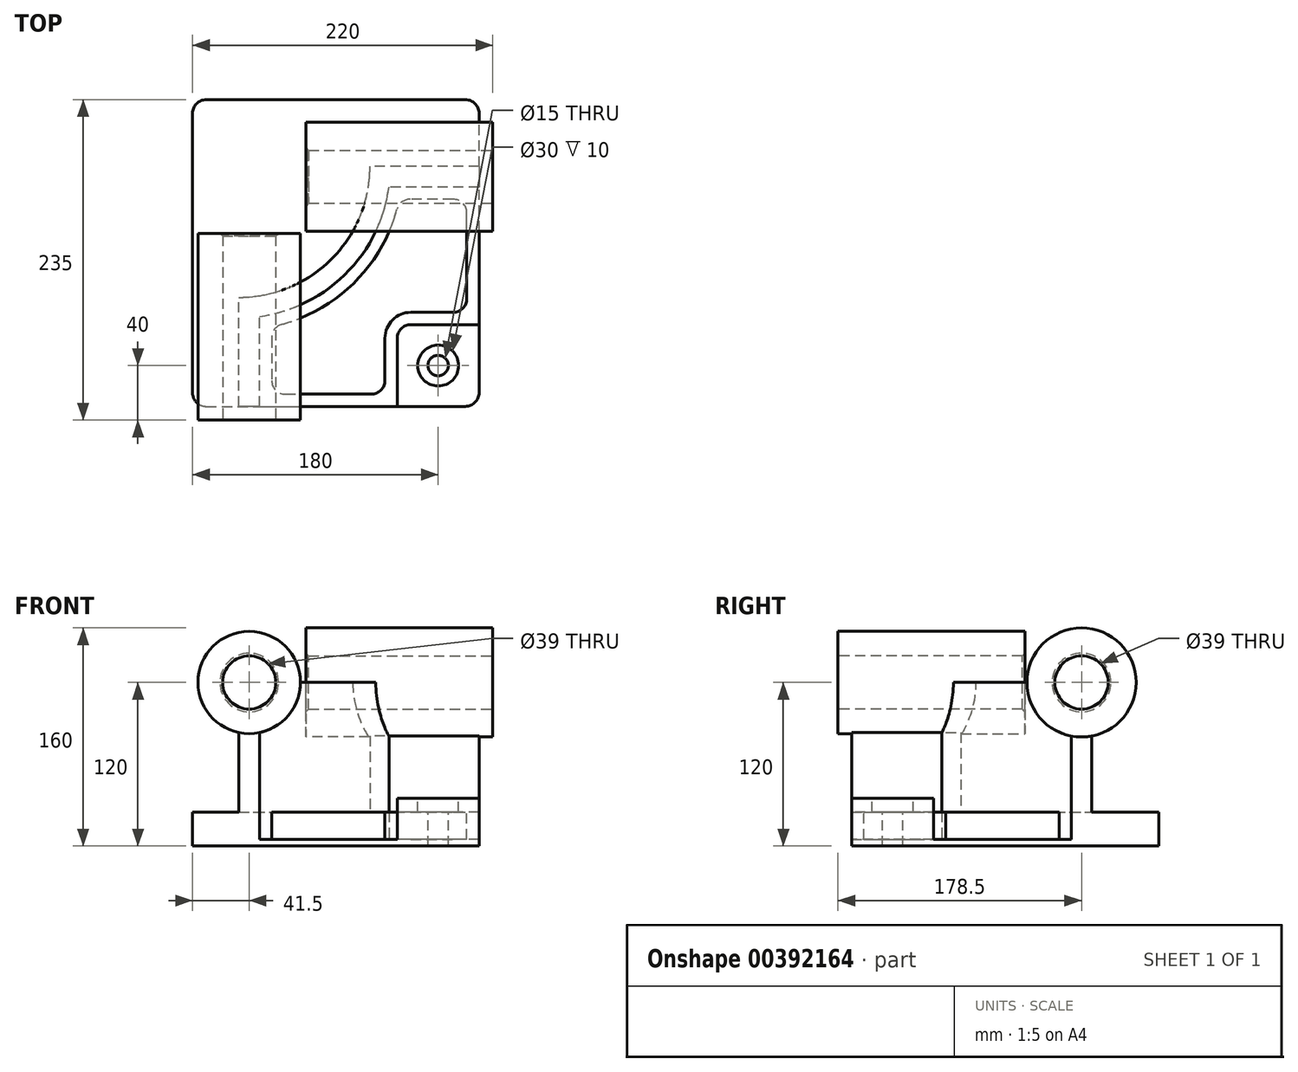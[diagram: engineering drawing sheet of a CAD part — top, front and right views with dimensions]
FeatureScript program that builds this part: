
annotation { "Feature Type Name" : "Feature", "Feature Type Description" : "" }
export const myFeature = defineFeature(function(context is Context, id is Id, definition is map)
    precondition{}
    {
        {
            var Q0;
            Q0=qCreatedBy(makeId("Top.planeOp"),FACE);
            var sketch = newSketch(context, id + "F0", { "sketchPlane" : qUnion([Q0])});
            skLineSegment(sketch, "E0.bottom", {"start": v(-105, -112.5) * mm, "end": v(105, -112.5) * mm});
            skLineSegment(sketch, "E0.top", {"start": v(-105, 112.5) * mm, "end": v(105, 112.5) * mm});
            skLineSegment(sketch, "E0.left", {"start": v(-105, -112.5) * mm, "end": v(-105, 112.5) * mm});
            skLineSegment(sketch, "E0.right", {"start": v(105, -112.5) * mm, "end": v(105, 112.5) * mm});
            skPoint(sketch, "E0.middle", {"position": v(0, 0) * mm});
            skSolve(sketch);
        }
        {
            var Q0;
            Q0=makeQuery(id+"F0.imprint","IMPRINT",FACE,{"disambiguationData":[TD([[makeQuery(id+"F0.imprint","IMPRINT",EDGE,{"derivedFrom":sQuery(id+"F0.wireOp",EDGE,"E0.bottom")}),1.0]])]});
            extrude(context, id + "F1", {"entities" : qUnion([Q0]), "depth" : 25 * mm});
        }
        {
            var Q0;
            Q0=makeQuery(id+"F1.opExtrude","CAP_FACE",FACE,{"disambiguationData":[OSD([sQuery(id+"F0.wireOp",EDGE,"E0.bottom"),sQuery(id+"F0.wireOp",EDGE,"E0.top"),sQuery(id+"F0.wireOp",EDGE,"E0.left"),sQuery(id+"F0.wireOp",EDGE,"E0.right")])],"isStart":false});
            var sketch = newSketch(context, id + "F2", { "sketchPlane" : qUnion([Q0])});
            skLineSegment(sketch, "E1", {"start": v(-71, -112.5) * mm, "end": v(-71, -32.5) * mm});
            skLineSegment(sketch, "E2", {"start": v(105, 63.5) * mm, "end": v(25, 63.5) * mm});
            skArc(sketch, "E3", {"start": v(-71, -32.5) * mm, "mid": v(-3.12, -4.38) * mm, "end": v(25, 63.5) * mm});
            skLineSegment(sketch, "E4", {"start": v(-71, 63.5) * mm, "end": v(25, 63.5) * mm, "construction": true});
            skLineSegment(sketch, "E5", {"start": v(-71, 63.5) * mm, "end": v(-71, -32.5) * mm, "construction": true});
            skLineSegment(sketch, "E6.0", {"start": v(105, 48.5) * mm, "end": v(38.98, 48.5) * mm});
            skArc(sketch, "E6.1", {"start": v(-56, -46.48) * mm, "mid": v(7.49, -14.99) * mm, "end": v(38.98, 48.5) * mm});
            skLineSegment(sketch, "E6.2", {"start": v(-56, -112.5) * mm, "end": v(-56, -46.48) * mm});
            skLineSegment(sketch, "E7.0", {"start": v(105, -112.5) * mm, "end": v(105, 112.5) * mm});
            skSolve(sketch);
        }
        {
            var Q0;
            {var subQ0=sQuery(id+"F2.wireOp",EDGE,"E3");Q0=makeQuery(id+"F2.imprint","IMPRINT",FACE,{"disambiguationData":[TD([[makeQuery(id+"F2.imprint","IMPRINT",EDGE,{"derivedFrom":subQ0}),-1.0]])]});}
            extrude(context, id + "F3", {"entities" : qUnion([Q0]), "operationType" : NewBodyOperationType.ADD, "depth" : 95 * mm});
        }
        {
            var Q0;
            {var subQ0=sQuery(id+"F0.wireOp",EDGE,"E0.bottom");Q0=makeQuery(id+"F3.boolean.opBoolean","MERGE",FACE,{"derivedFrom":[makeQuery(id+"F1.opExtrude","SWEPT_FACE",FACE,{"disambiguationData":[OSD([subQ0])]}),makeQuery(id+"F3.opExtrude","SWEPT_FACE",FACE,{"disambiguationData":[OSD([subQ0])]})]});}
            var sketch = newSketch(context, id + "F4", { "sketchPlane" : qUnion([Q0])});
            skCircle(sketch, "E8", {"center": v(-63.5, 120) * mm, "radius": 37.5 * mm});
            skSolve(sketch);
        }
        {
            var Q0;
            Q0 = qSketchRegion(id + "F4", true);
            var Q1;
            {var subQ1=sQuery(id+"F0.wireOp",EDGE,"E0.bottom");var subQ6=makeQuery(id+"F3.opExtrude","CAP_EDGE",EDGE,{"disambiguationData":[OSD([subQ1])],"isStart":false});Q1=makeQuery(id+"F4.imprint","IMPRINT",FACE,{"disambiguationData":[TD([[makeQuery(id+"F4.imprint","IMPRINT",EDGE,{"derivedFrom":subQ6}),1.0]])]});}
            extrude(context, id + "F5", {"entities" : qUnion([Q0, Q1]), "operationType" : NewBodyOperationType.ADD, "depth" : 10 * mm, "hasSecondDirection" : true, "secondDirectionOppositeDirection" : true, "secondDirectionDepth" : (137 - 10) * mm});
        }
        {
            var Q0;
            Q0=makeQuery(id+"F3.boolean.opBoolean","MERGE",FACE,{"derivedFrom":[makeQuery(id+"F1.opExtrude","SWEPT_FACE",FACE,{"disambiguationData":[OSD([sQuery(id+"F0.wireOp",EDGE,"E0.right")])]}),makeQuery(id+"F3.opExtrude","SWEPT_FACE",FACE,{"disambiguationData":[OSD([sQuery(id+"F2.wireOp",EDGE,"E7.0")])]})]});
            var sketch = newSketch(context, id + "F6", { "sketchPlane" : qUnion([Q0])});
            skCircle(sketch, "E9", {"center": v(56, 120) * mm, "radius": 40 * mm});
            skSolve(sketch);
        }
        {
            var Q0;
            Q0 = qSketchRegion(id + "F6", true);
            extrude(context, id + "F7", {"entities" : qUnion([Q0]), "operationType" : NewBodyOperationType.ADD, "depth" : 10 * mm, "hasSecondDirection" : true, "secondDirectionOppositeDirection" : true, "secondDirectionDepth" : (137 - 10) * mm});
        }
        {
            var Q0;
            {var subQ0=sQuery(id+"F0.wireOp",EDGE,"E0.right");var subQ1=sQuery(id+"F0.wireOp",EDGE,"E0.bottom");Q0=makeQuery(id+"F3.boolean.opBoolean","SPLIT",FACE,{"disambiguationData":[TD([makeQuery(id+"F3.opExtrude","SWEPT_FACE",FACE,{"disambiguationData":[OSD([sQuery(id+"F2.wireOp",EDGE,"E6.0")])]})])],"derivedFrom":makeQuery(id+"F1.opExtrude","CAP_FACE",FACE,{"disambiguationData":[OSD([subQ1,sQuery(id+"F0.wireOp",EDGE,"E0.top"),sQuery(id+"F0.wireOp",EDGE,"E0.left"),subQ0])],"isStart":false})});}
            var sketch = newSketch(context, id + "F8", { "sketchPlane" : qUnion([Q0])});
            skLineSegment(sketch, "E10.bottom", {"start": v(105, -52.5) * mm, "end": v(45, -52.5) * mm});
            skLineSegment(sketch, "E10.top", {"start": v(105, -112.5) * mm, "end": v(45, -112.5) * mm});
            skLineSegment(sketch, "E10.left", {"start": v(105, -52.5) * mm, "end": v(105, -112.5) * mm});
            skLineSegment(sketch, "E10.right", {"start": v(45, -52.5) * mm, "end": v(45, -112.5) * mm});
            skSolve(sketch);
        }
        {
            var Q0;
            Q0=makeQuery(id+"F8.imprint","IMPRINT",FACE,{"disambiguationData":[TD([[makeQuery(id+"F8.imprint","IMPRINT",EDGE,{"derivedFrom":sQuery(id+"F8.wireOp",EDGE,"E10.bottom")}),1.0]])]});
            extrude(context, id + "F9", {"entities" : qUnion([Q0]), "operationType" : NewBodyOperationType.ADD, "depth" : 10 * mm});
        }
        {
            var Q0;
            Q0=makeQuery(id+"F9.opExtrude","SWEPT_EDGE",EDGE,{"disambiguationData":[OSD([sQuery(id+"F8.wireOp",EDGE,"E10.bottom"),sQuery(id+"F8.wireOp",EDGE,"E10.right")])]});
            fillet(context, id + "F10", {"entities" : qUnion([Q0]), "radius" : 10 * mm, "tangentPropagation" : true, "allowEdgeOverflow" : false});
        }
        {
            var Q0;
            {var subQ0=sQuery(id+"F0.wireOp",EDGE,"E0.right");var subQ1=sQuery(id+"F0.wireOp",EDGE,"E0.bottom");Q0=makeQuery(id+"F3.boolean.opBoolean","SPLIT",FACE,{"disambiguationData":[TD([makeQuery(id+"F3.opExtrude","SWEPT_FACE",FACE,{"disambiguationData":[OSD([sQuery(id+"F2.wireOp",EDGE,"E6.0")])]})])],"derivedFrom":makeQuery(id+"F1.opExtrude","CAP_FACE",FACE,{"disambiguationData":[OSD([subQ1,sQuery(id+"F0.wireOp",EDGE,"E0.top"),sQuery(id+"F0.wireOp",EDGE,"E0.left"),subQ0])],"isStart":false})});}
            var sketch = newSketch(context, id + "F11", { "sketchPlane" : qUnion([Q0])});
            skArc(sketch, "E11.0", {"start": v(36, -62.5) * mm, "mid": v(41.56, -49.06) * mm, "end": v(55, -43.5) * mm});
            skLineSegment(sketch, "E11.1", {"start": v(36, -103.5) * mm, "end": v(36, -62.5) * mm});
            skLineSegment(sketch, "E11.2", {"start": v(55, -43.5) * mm, "end": v(96, -43.5) * mm});
            skLineSegment(sketch, "E11.3", {"start": v(-47, -103.5) * mm, "end": v(36, -103.5) * mm});
            skLineSegment(sketch, "E11.4", {"start": v(96, -43.5) * mm, "end": v(96, 39.5) * mm});
            skLineSegment(sketch, "E11.5", {"start": v(96, 39.5) * mm, "end": v(46.58, 39.5) * mm});
            skArc(sketch, "E11.6", {"start": v(46.58, 39.5) * mm, "mid": v(13.85, -21.35) * mm, "end": v(-47, -54.08) * mm});
            skLineSegment(sketch, "E11.7", {"start": v(-47, -54.08) * mm, "end": v(-47, -103.5) * mm});
            skSolve(sketch);
        }
        {
            var Q0;
            Q0=makeQuery(id+"F11.imprint","IMPRINT",FACE,{"disambiguationData":[TD([[makeQuery(id+"F11.imprint","IMPRINT",EDGE,{"derivedFrom":sQuery(id+"F11.wireOp",EDGE,"E11.0")}),1.0]])]});
            extrude(context, id + "F12", {"entities" : qUnion([Q0]), "operationType" : NewBodyOperationType.REMOVE, "oppositeDirection" : true, "depth" : (25 - 5) * mm});
        }
        {
            var Q0;
            Q0=makeQuery(id+"F9.opExtrude","CAP_FACE",FACE,{"disambiguationData":[OSD([sQuery(id+"F8.wireOp",EDGE,"E10.bottom"),sQuery(id+"F8.wireOp",EDGE,"E10.top"),sQuery(id+"F8.wireOp",EDGE,"E10.left"),sQuery(id+"F8.wireOp",EDGE,"E10.right")])],"isStart":false});
            var sketch = newSketch(context, id + "F13", { "sketchPlane" : qUnion([Q0])});
            skCircle(sketch, "E12", {"center": v(75, -82.5) * mm, "radius": 15 * mm});
            skPoint(sketch, "E12.centerSnap0", {"position": v(75, -112.5) * mm});
            skPoint(sketch, "E12.centerSnap1", {"position": v(105, -82.5) * mm});
            skSolve(sketch);
        }
        {
            var Q0;
            Q0=sQuery(id+"F13.wireOp",VERTEX,"E12.center");
            var Q1;
            Q1=makeQuery(id+"F1.opExtrude","SWEPT_BODY",BODY,{"disambiguationData":[OSD([sQuery(id+"F0.wireOp",EDGE,"E0.bottom"),sQuery(id+"F0.wireOp",EDGE,"E0.top"),sQuery(id+"F0.wireOp",EDGE,"E0.left"),sQuery(id+"F0.wireOp",EDGE,"E0.right")])]});
            hole(context, id + "F14", {"style" : HoleStyle.C_BORE, "endStyle" : HoleEndStyle.THROUGH, "holeDiameter" : 15 * mm, "cBoreDiameter" : 30 * mm, "cBoreDepth" : 10 * mm, "isTappedThrough" : true, "tappedDepth" : 12.7 * mm, "tapClearance" : 3, "locations" : qUnion([Q0]), "scope" : qUnion([Q1])});
        }
        {
            var Q0;
            Q0=makeQuery(id+"F12.boolean.opBoolean","COPY",EDGE,{"derivedFrom":makeQuery(id+"F12.opExtrude","SWEPT_EDGE",EDGE,{"disambiguationData":[OSD([sQuery(id+"F11.wireOp",EDGE,"E11.6"),sQuery(id+"F11.wireOp",EDGE,"E11.7")])]})});
            var Q1;
            Q1=makeQuery(id+"F12.boolean.opBoolean","COPY",EDGE,{"derivedFrom":makeQuery(id+"F12.opExtrude","SWEPT_EDGE",EDGE,{"disambiguationData":[OSD([sQuery(id+"F11.wireOp",EDGE,"E11.5"),sQuery(id+"F11.wireOp",EDGE,"E11.6")])]})});
            var Q2;
            Q2=makeQuery(id+"F12.boolean.opBoolean","COPY",EDGE,{"derivedFrom":makeQuery(id+"F12.opExtrude","SWEPT_EDGE",EDGE,{"disambiguationData":[OSD([sQuery(id+"F11.wireOp",EDGE,"E11.3"),sQuery(id+"F11.wireOp",EDGE,"E11.7")])]})});
            var Q3;
            Q3=makeQuery(id+"F12.boolean.opBoolean","COPY",EDGE,{"derivedFrom":makeQuery(id+"F12.opExtrude","SWEPT_EDGE",EDGE,{"disambiguationData":[OSD([sQuery(id+"F11.wireOp",EDGE,"E11.4"),sQuery(id+"F11.wireOp",EDGE,"E11.5")])]})});
            var Q4;
            Q4=makeQuery(id+"F12.boolean.opBoolean","COPY",EDGE,{"derivedFrom":makeQuery(id+"F12.opExtrude","SWEPT_EDGE",EDGE,{"disambiguationData":[OSD([sQuery(id+"F11.wireOp",EDGE,"E11.2"),sQuery(id+"F11.wireOp",EDGE,"E11.4")])]})});
            var Q5;
            Q5=makeQuery(id+"F12.boolean.opBoolean","COPY",EDGE,{"derivedFrom":makeQuery(id+"F12.opExtrude","SWEPT_EDGE",EDGE,{"disambiguationData":[OSD([sQuery(id+"F11.wireOp",EDGE,"E11.1"),sQuery(id+"F11.wireOp",EDGE,"E11.3")])]})});
            fillet(context, id + "F15", {"entities" : qUnion([Q0, Q1, Q2, Q3, Q4, Q5]), "radius" : 10 * mm, "tangentPropagation" : true, "allowEdgeOverflow" : false});
        }
        {
            var Q0;
            Q0=makeQuery(id+"F9.boolean.opBoolean","MERGE",EDGE,{"derivedFrom":[makeQuery(id+"F1.opExtrude","SWEPT_EDGE",EDGE,{"disambiguationData":[OSD([sQuery(id+"F0.wireOp",EDGE,"E0.bottom"),sQuery(id+"F0.wireOp",EDGE,"E0.right")])]}),makeQuery(id+"F9.opExtrude","SWEPT_EDGE",EDGE,{"disambiguationData":[OSD([sQuery(id+"F8.wireOp",EDGE,"E10.top"),sQuery(id+"F8.wireOp",EDGE,"E10.left")])]})]});
            var Q1;
            Q1=makeQuery(id+"F1.opExtrude","SWEPT_EDGE",EDGE,{"disambiguationData":[OSD([sQuery(id+"F0.wireOp",EDGE,"E0.bottom"),sQuery(id+"F0.wireOp",EDGE,"E0.left")])]});
            var Q2;
            Q2=makeQuery(id+"F1.opExtrude","SWEPT_EDGE",EDGE,{"disambiguationData":[OSD([sQuery(id+"F0.wireOp",EDGE,"E0.top"),sQuery(id+"F0.wireOp",EDGE,"E0.right")])]});
            var Q3;
            Q3=makeQuery(id+"F1.opExtrude","SWEPT_EDGE",EDGE,{"disambiguationData":[OSD([sQuery(id+"F0.wireOp",EDGE,"E0.top"),sQuery(id+"F0.wireOp",EDGE,"E0.left")])]});
            fillet(context, id + "F16", {"entities" : qUnion([Q0, Q1, Q2, Q3]), "radius" : 10 * mm, "tangentPropagation" : true, "allowEdgeOverflow" : false});
        }
        {
            var Q0;
            Q0=makeQuery(id+"F5.opExtrude","CAP_FACE",FACE,{"disambiguationData":[OSD([sQuery(id+"F4.wireOp",EDGE,"E8")])],"isStart":false});
            var sketch = newSketch(context, id + "F17", { "sketchPlane" : qUnion([Q0])});
            skCircle(sketch, "E13", {"center": v(-63.5, 120) * mm, "radius": 19.5 * mm});
            skSolve(sketch);
        }
        {
            var Q0;
            Q0 = qSketchRegion(id + "F17", true);
            var Q1;
            Q1=makeQuery(id+"F17.imprint","IMPRINT",FACE,{"disambiguationData":[TD([[makeQuery(id+"F17.imprint","IMPRINT",EDGE,{"derivedFrom":sQuery(id+"F17.wireOp",EDGE,"E13")}),1.0]])]});
            extrude(context, id + "F18", {"entities" : qUnion([Q0, Q1]), "operationType" : NewBodyOperationType.REMOVE, "endBound" : BoundingType.THROUGH_ALL, "oppositeDirection" : true, "depth" : 25.4 * mm});
        }
        {
            var Q0;
            Q0=makeQuery(id+"F7.opExtrude","CAP_FACE",FACE,{"disambiguationData":[OSD([sQuery(id+"F6.wireOp",EDGE,"E9")])],"isStart":false});
            var sketch = newSketch(context, id + "F19", { "sketchPlane" : qUnion([Q0])});
            skCircle(sketch, "E14", {"center": v(56, 120) * mm, "radius": 19.5 * mm});
            skSolve(sketch);
        }
        {
            var Q0;
            Q0 = qSketchRegion(id + "F19", true);
            var Q1;
            Q1=makeQuery(id+"F19.imprint","IMPRINT",FACE,{"disambiguationData":[TD([[makeQuery(id+"F19.imprint","IMPRINT",EDGE,{"derivedFrom":sQuery(id+"F19.wireOp",EDGE,"E14")}),1.0]])]});
            extrude(context, id + "F20", {"entities" : qUnion([Q0, Q1]), "operationType" : NewBodyOperationType.REMOVE, "endBound" : BoundingType.THROUGH_ALL, "oppositeDirection" : true, "depth" : 25.4 * mm});
        }
        {
            var Q0;
            Q0=makeQuery(id+"F18.boolean.opBoolean","COPY",EDGE,{"derivedFrom":makeQuery(id+"F18.opExtrude","CAP_EDGE",EDGE,{"disambiguationData":[OSD([sQuery(id+"F17.wireOp",EDGE,"E13")])],"isStart":true})});
            var Q1;
            Q1=makeQuery(id+"F20.boolean.opBoolean","COPY",EDGE,{"derivedFrom":makeQuery(id+"F20.opExtrude","CAP_EDGE",EDGE,{"disambiguationData":[OSD([sQuery(id+"F19.wireOp",EDGE,"E14")])],"isStart":true})});
            var Q2;
            Q2=makeQuery(id+"F20.boolean.opBoolean","INTERSECT",EDGE,{"derivedFrom":[makeQuery(id+"F7.opExtrude","CAP_FACE",FACE,{"disambiguationData":[OSD([sQuery(id+"F6.wireOp",EDGE,"E9")])],"isStart":true}),makeQuery(id+"F20.opExtrude","SWEPT_FACE",FACE,{"disambiguationData":[OSD([sQuery(id+"F19.wireOp",EDGE,"E14")])]})]});
            var Q3;
            Q3=makeQuery(id+"F18.boolean.opBoolean","INTERSECT",EDGE,{"derivedFrom":[makeQuery(id+"F5.opExtrude","CAP_FACE",FACE,{"disambiguationData":[OSD([sQuery(id+"F4.wireOp",EDGE,"E8")])],"isStart":true}),makeQuery(id+"F18.opExtrude","SWEPT_FACE",FACE,{"disambiguationData":[OSD([sQuery(id+"F17.wireOp",EDGE,"E13")])]})]});
            chamfer(context, id + "F21", {"entities" : qUnion([Q0, Q1, Q2, Q3]), "width" : 2 * mm, "tangentPropagation" : true});
        }
    });
